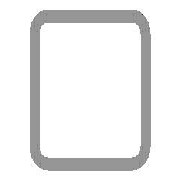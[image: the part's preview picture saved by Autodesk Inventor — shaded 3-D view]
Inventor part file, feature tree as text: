
AUTODESK INVENTOR PART (.ipt)
format: ipt  version: 2025 (Build 290162010, 162A)  size: 133,120 bytes
history: native  units: mm (DEFAULTED — no unit token found)
features: other x4, sketch x1, plane x1
ambient origin geometry x8: Origin, YZ Plane, XZ Plane, XY Plane, X Axis, Y Axis, Z Axis, Center Point
bodies: Solid1 (feature_tree), Body (feature_tree)
feature tree (6):
  parser-record x1  (decoder bookkeeping rows leaked as tree rows — omitted from the tree; the rows remain in map.json)
  other  "Driven Length"
  other  "Start Plane"
  other  "End Plane"
  sketch  "Sketch3"  dims[d3=898.0mm d4=0.0mm d7=4.0mm d9=40.0mm d11=40.0mm d12=2.0mm d13=-0.0mm d14=898.0mm d15=20.0mm d16=20.0mm d17=90.0deg d18=898.0mm]
  plane  "Work Plane3"
